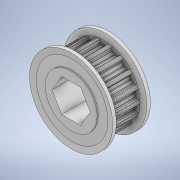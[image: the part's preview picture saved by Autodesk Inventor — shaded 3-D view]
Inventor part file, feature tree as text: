
AUTODESK INVENTOR PART (.ipt)
format: ipt  version: 2020 (Build 240168000, 168)  size: 518,144 bytes
history: native  units: in
note: dims shown in document units (in); Inventor stores cm internally (conversion verified against a paired STEP export)
features: mirror x1
ambient origin geometry x8: Origin, YZ Plane, XZ Plane, XY Plane, X Axis, Y Axis, Z Axis, Center Point
bodies: Solid1 (feature_tree)
feature tree (1):
  mirror  "Mirror1"
